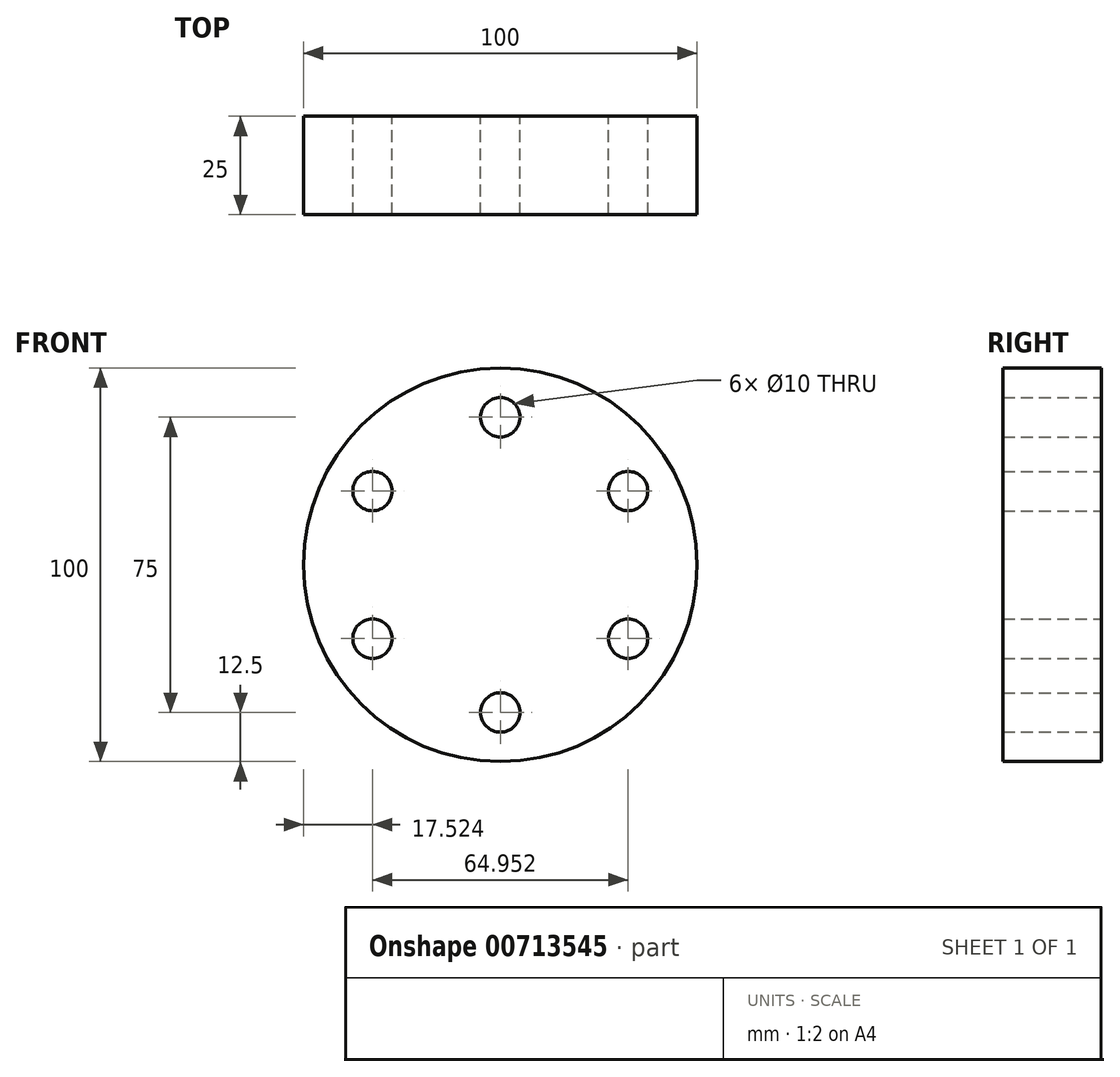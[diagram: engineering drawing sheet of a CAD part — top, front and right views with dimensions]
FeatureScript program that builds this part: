
annotation { "Feature Type Name" : "Feature", "Feature Type Description" : "" }
export const myFeature = defineFeature(function(context is Context, id is Id, definition is map)
    precondition{}
    {
        {
            var Q0;
            Q0=qCreatedBy(makeId("Front.planeOp"),FACE);
            var sketch = newSketch(context, id + "F0", { "sketchPlane" : qUnion([Q0])});
            skCircle(sketch, "E0", {"center": v(0, 0) * mm, "radius": 50 * mm});
            skCircle(sketch, "E1", {"center": v(0, 37.5) * mm, "radius": 5 * mm});
            skCircle(sketch, "E2", {"center": v(0, 0) * mm, "radius": 37.5 * mm, "construction": true});
            skCircle(sketch, "E3.1.0", {"center": v(-32.48, 18.75) * mm, "radius": 5 * mm});
            skCircle(sketch, "E3.2.0", {"center": v(-32.48, -18.75) * mm, "radius": 5 * mm});
            skCircle(sketch, "E3.3.0", {"center": v(0, -37.5) * mm, "radius": 5 * mm});
            skCircle(sketch, "E3.4.0", {"center": v(32.48, -18.75) * mm, "radius": 5 * mm});
            skCircle(sketch, "E3.5.0", {"center": v(32.48, 18.75) * mm, "radius": 5 * mm});
            skSolve(sketch);
        }
        {
            var Q0;
            Q0 = qSketchRegion(id + "F0", true);
            extrude(context, id + "F1", {"entities" : qUnion([Q0]), "depth" : 25 * mm, "offsetDistance" : 25 * mm});
        }
    });
